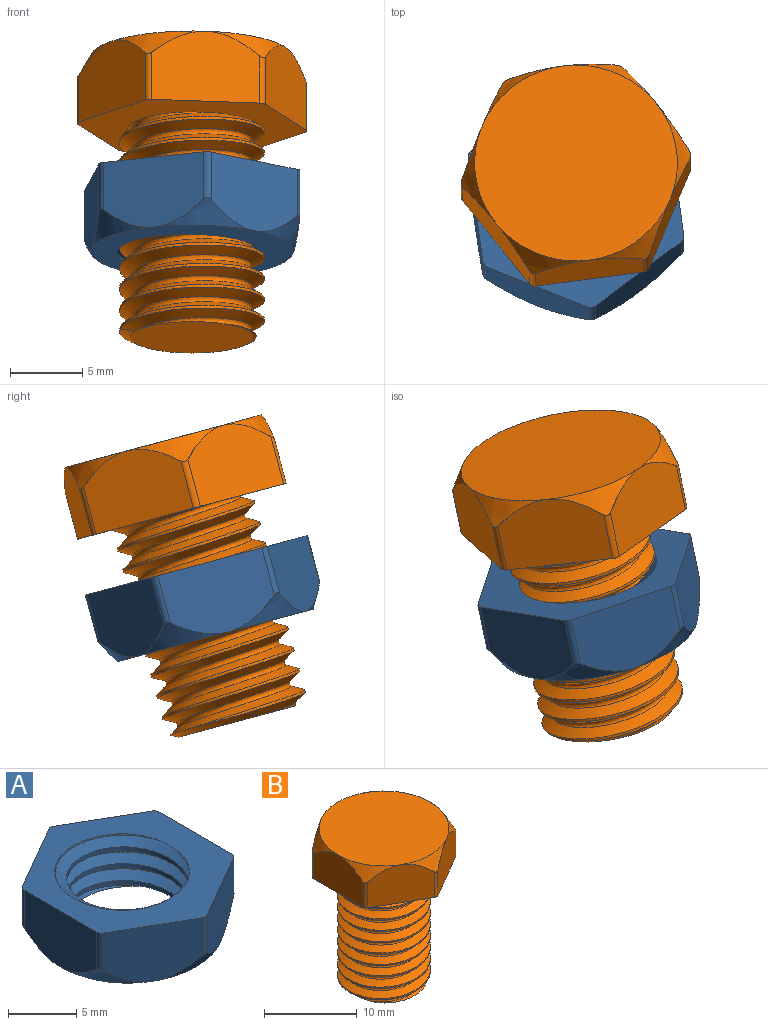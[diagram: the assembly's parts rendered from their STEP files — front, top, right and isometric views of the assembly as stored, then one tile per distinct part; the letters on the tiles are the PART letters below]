
ASSEMBLY  parts=2 mates=1
PART A: 24 faces, bbox 16.3x16.5x6.8 mm
  f0: plane 14.44x14.44mm, normal (0,0,-1), area 79.5mm2, adj f8,f9,f10,f11,f12,f13,f14,f15
  f1: plane 7.51x5mm, normal (1,0,0), area 33.3mm2, adj f7,f13,f17,f18,f22
  f2: plane 6.51x5mm, normal (0.5,0.87,0), area 33.3mm2, adj f7,f16,f17,f18,f19
  f3: plane 6.51x5mm, normal (-0.5,0.87,0), area 33.3mm2, adj f7,f15,f16,f19,f20
  f4: plane 7.51x5mm, normal (-1,0,0), area 33.3mm2, adj f7,f14,f15,f20,f23
  f5: plane 6.51x5mm, normal (-0.5,-0.87,0), area 33.3mm2, adj f7,f12,f14,f21,f23
  f6: plane 6.51x5mm, normal (0.5,-0.87,0), area 33.3mm2, adj f7,f12,f13,f21,f22
  f7: plane 16.45x14.44mm, normal (0,0,1), area 95.2mm2, adj f1,f2,f3,f4,f5,f6,f8,f9
  f8: bspline ~12.27x10.62mm, area 96.1mm2, adj f0,f7,f10,f11
  f9: bspline ~12.27x10.62mm, area 96.5mm2, adj f0,f7,f10,f11
  f10: bspline ~12.42x10.76mm, area 24.3mm2, adj f0,f7,f8,f9
  f11: cylinder r=4.5mm len=9mm, axis (0,0,-1), area 34.8mm2, adj f0,f7,f8,f9
  f12: cone r=7mm half-angle=30deg, axis (0,0,1), area 5.2mm2, adj f0,f5,f6,f21
  f13: cone r=7mm half-angle=30deg, axis (0,0,1), area 5.2mm2, adj f0,f1,f6,f22
  f14: cone r=7mm half-angle=30deg, axis (0,0,1), area 5.2mm2, adj f0,f4,f5,f23
  f15: cone r=7mm half-angle=30deg, axis (0,0,1), area 5.2mm2, adj f0,f3,f4,f20
  f16: cone r=7mm half-angle=30deg, axis (0,0,1), area 5.2mm2, adj f0,f2,f3,f19
  f17: cone r=7mm half-angle=30deg, axis (0,0,1), area 5.2mm2, adj f0,f1,f2,f18
  f18: cylinder r=0.5mm len=3.37mm, axis (0,0,1), area 1.8mm2, adj f1,f2,f7,f17
  f19: cylinder r=0.5mm len=3.37mm, axis (0,0,1), area 1.8mm2, adj f2,f3,f7,f16
  f20: cylinder r=0.5mm len=3.37mm, axis (0,0,1), area 1.8mm2, adj f3,f4,f7,f15
  f21: cylinder r=0.5mm len=3.37mm, axis (0,0,1), area 1.8mm2, adj f5,f6,f7,f12
  f22: cylinder r=0.5mm len=3.37mm, axis (0,0,1), area 1.8mm2, adj f1,f6,f7,f13
  f23: cylinder r=0.5mm len=3.37mm, axis (0,0,1), area 1.8mm2, adj f4,f5,f7,f14
PART B: 26 faces, bbox 16.3x16.4x21 mm
  f0: plane 8.56x8.43mm, normal (0,0,-1), area 55.9mm2, adj f22,f23,f24,f25
  f1: cylinder r=5mm len=14.63mm, axis (0,0,1), area 43.4mm2, adj f8,f23,f24,f25
  f2: plane 7.51x5mm, normal (1,0,0), area 33.3mm2, adj f8,f9,f14,f16,f21
  f3: plane 6.51x5mm, normal (0.5,0.87,0), area 33.3mm2, adj f8,f13,f14,f16,f17
  f4: plane 6.51x5mm, normal (-0.5,0.87,0), area 33.3mm2, adj f8,f12,f13,f17,f18
  f5: plane 7.51x5mm, normal (-1,0,0), area 33.3mm2, adj f8,f11,f12,f18,f19
  f6: plane 6.51x5mm, normal (-0.5,-0.87,0), area 33.3mm2, adj f8,f10,f11,f19,f20
  f7: plane 6.51x5mm, normal (0.5,-0.87,0), area 33.3mm2, adj f8,f9,f10,f20,f21
  f8: plane 16.43x14.42mm, normal (0,0,-1), area 104.9mm2, adj f1,f2,f3,f4,f5,f6,f7,f16
  f9: cone r=9.04mm half-angle=30deg, axis (0,0,-1), area 5.2mm2, adj f2,f7,f15,f21
  f10: cone r=9.04mm half-angle=30deg, axis (0,0,-1), area 5.2mm2, adj f6,f7,f15,f20
  f11: cone r=9.04mm half-angle=30deg, axis (0,0,-1), area 5.2mm2, adj f5,f6,f15,f19
  f12: cone r=9.04mm half-angle=30deg, axis (0,0,-1), area 5.2mm2, adj f4,f5,f15,f18
  f13: cone r=9.04mm half-angle=30deg, axis (0,0,-1), area 5.2mm2, adj f3,f4,f15,f17
  f14: cone r=9.04mm half-angle=30deg, axis (0,0,-1), area 5.2mm2, adj f2,f3,f15,f16
  f15: plane 14x14mm, normal (0,0,1), area 153.9mm2, adj f9,f10,f11,f12,f13,f14
  f16: cylinder r=0.5mm len=3.37mm, axis (0,0,-1), area 1.8mm2, adj f2,f3,f8,f14
  f17: cylinder r=0.5mm len=3.37mm, axis (0,0,-1), area 1.8mm2, adj f3,f4,f8,f13
  f18: cylinder r=0.5mm len=3.37mm, axis (0,0,-1), area 1.8mm2, adj f4,f5,f8,f12
  f19: cylinder r=0.5mm len=3.37mm, axis (0,0,-1), area 1.8mm2, adj f5,f6,f8,f11
  f20: cylinder r=0.5mm len=3.37mm, axis (0,0,-1), area 1.8mm2, adj f6,f7,f8,f10
  f21: cylinder r=0.5mm len=3.37mm, axis (0,0,-1), area 1.8mm2, adj f2,f7,f8,f9
  f22: bspline ~16.13x9.67mm, area 109.3mm2, adj f0,f8,f23,f24
  f23: bspline ~16.22x11.55mm, area 267mm2, adj f0,f1,f8,f22,f25
  f24: bspline ~15.72x11.55mm, area 267.7mm2, adj f0,f1,f8,f22,f25
  f25: cone r=5mm half-angle=63.4deg, axis (0,0,1), area 9.9mm2, adj f0,f1,f23,f24
PLACE A rot(axis=(-0.06,0.13,0.99),128.3deg) t=(12.31,-17.09,-4.95)mm
PLACE B rot(axis=(-0.11,0.13,0.99),98.6deg) t=(12.31,-16.09,-1.21)mm fixed
MATE cylindrical B.f9 <-> A.f11  axis (0,0.26,0.97) through (12.31,-14.79,3.62)mm
